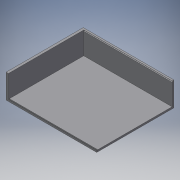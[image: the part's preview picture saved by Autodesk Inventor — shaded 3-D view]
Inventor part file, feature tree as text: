
AUTODESK INVENTOR PART (.ipt)
format: ipt  version: 2016 SP2 (Build 200236200, 236)  size: 113,664 bytes
history: native  units: mm
features: reference x5, extrude x2, sketch x2
ambient origin geometry x8: Origin, YZ Plane, XZ Plane, XY Plane, X Axis, Y Axis, Z Axis, Center Point
bodies: Volumenkörper1 (feature_tree)
feature tree (9):
  extrude  "Extrusion1"  Depth=2.0mm
  extrude  "Extrusion2"  Depth=2.5mm
  sketch  "Skizze1"  dims[d2=0.1mm d4=2.0mm]
  reference  "Referenz1"
  reference  "Referenz2"
  reference  "Referenz3"
  reference  "Referenz4"
  reference  "Referenz5"
  sketch  "Skizze2"  dims[d6=1.1mm d8=0.1mm d9=0.1mm d10=0.15mm d11=2.0mm d12=95.0mm d13=0.0mm d14=2.5mm d15=0.0mm]
